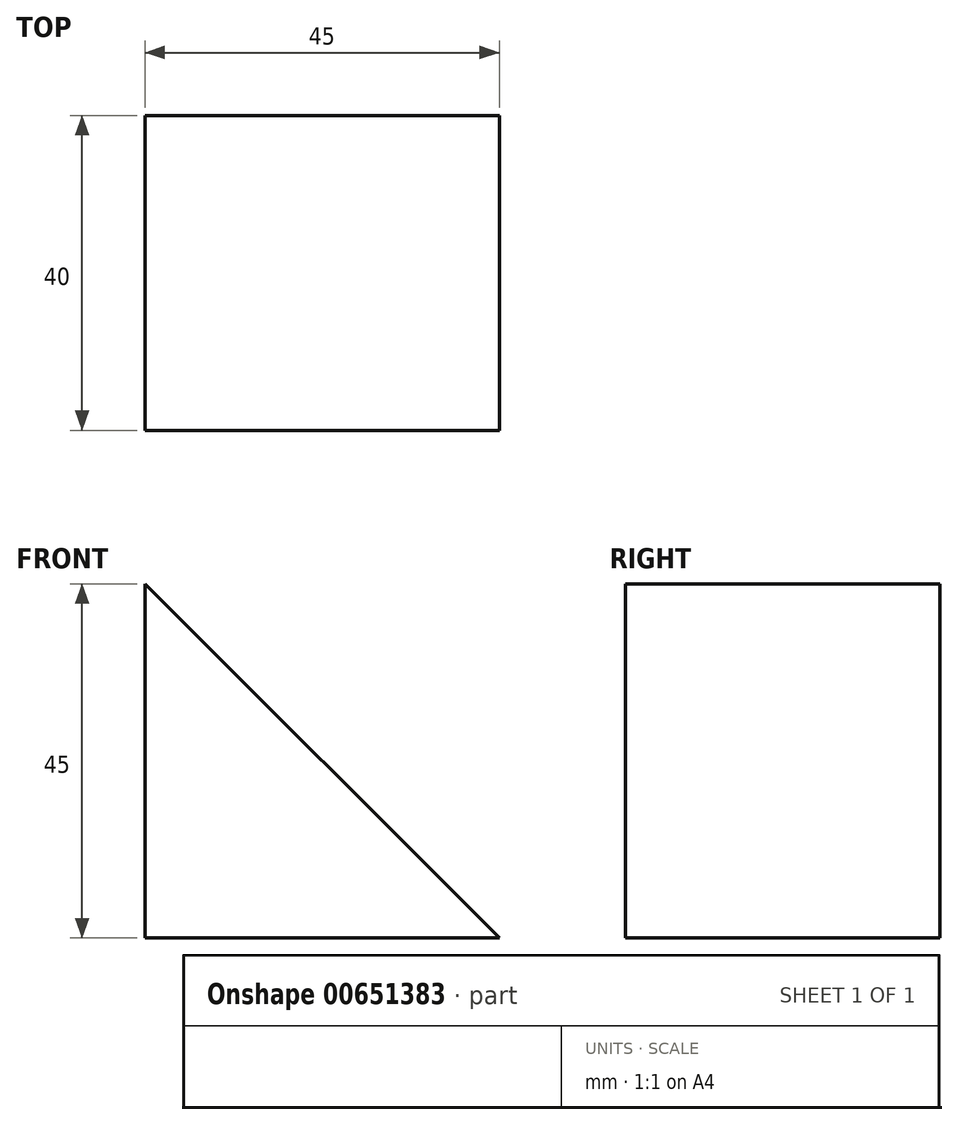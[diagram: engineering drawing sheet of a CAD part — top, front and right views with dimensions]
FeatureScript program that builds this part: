
annotation { "Feature Type Name" : "Feature", "Feature Type Description" : "" }
export const myFeature = defineFeature(function(context is Context, id is Id, definition is map)
    precondition{}
    {
        {
            var Q0;
            Q0=qCreatedBy(makeId("Front.planeOp"),FACE);
            var sketch = newSketch(context, id + "F0", { "sketchPlane" : qUnion([Q0])});
            skLineSegment(sketch, "E0", {"start": v(0, 0) * mm, "end": v(0, 45) * mm});
            skLineSegment(sketch, "E1", {"start": v(0, 45) * mm, "end": v(45, 0) * mm});
            skLineSegment(sketch, "E2", {"start": v(45, 0) * mm, "end": v(0, 0) * mm});
            skSolve(sketch);
        }
        {
            var Q0;
            Q0 = qSketchRegion(id + "F0", true);
            extrude(context, id + "F1", {"entities" : qUnion([Q0]), "depth" : 40 * mm, "offsetDistance" : 25 * mm});
        }
    });
